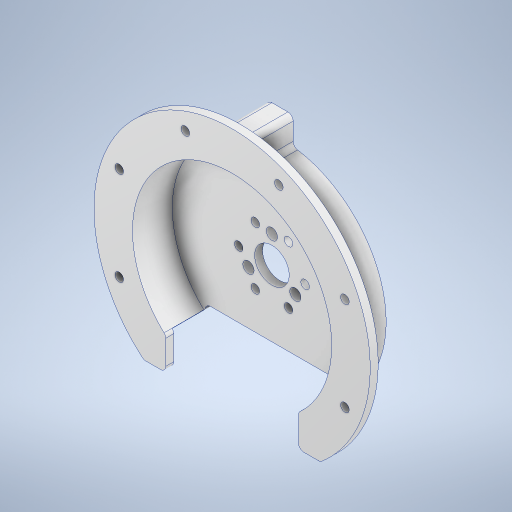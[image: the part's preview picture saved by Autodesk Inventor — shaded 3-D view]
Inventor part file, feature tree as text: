
AUTODESK INVENTOR PART (.ipt)
format: ipt  version: 2024.3 (Build 283343000, 343)  size: 454,656 bytes
history: native  units: mm
features: sketch x11, extrude x8, hole x3, fillet x2
ambient origin geometry x8: Origin, YZ Plane, XZ Plane, XY Plane, X Axis, Y Axis, Z Axis, Center Point
bodies: Body1 (feature_tree)
feature tree (24):
  extrude  "押し出し6"  Depth=80.0mm
  hole  "穴4"  [1 undecoded]
  hole  "穴5"  [1 undecoded]
  extrude  "押し出し7"  TaperAngle=30.0deg  [1 undecoded]
  extrude  "押し出し8"  Depth=60.0mm TaperAngle=360.0deg
  extrude  "押し出し9"  Depth=20.4mm
  hole  "穴6"  [1 undecoded]
  extrude  "押し出し10"  Depth=13.0mm
  extrude  "押し出し11"  TaperAngle=0.0deg  [1 undecoded]
  fillet  "フィレット3"  Radius=104.0mm
  extrude  "押し出し12"  Depth=3.0mm TaperAngle=0.0deg
  extrude  "押し出し13"  Depth=75.0mm
  fillet  "フィレット6"  Radius=15.0mm
  sketch  "スケッチ9"
  sketch  "スケッチ10"
  sketch  "スケッチ11"
  sketch  "スケッチ12"
  sketch  "スケッチ13"
  sketch  "スケッチ14"
  sketch  "スケッチ15"
  sketch  "スケッチ16"
  sketch  "スケッチ17"
  sketch  "スケッチ18"
  sketch  "スケッチ19"
note: 5 required parameter values undecoded (feature->parameter linkage not recoverable at this tier; creation-order binding heuristic only, values carry confidence <= 0.55)
